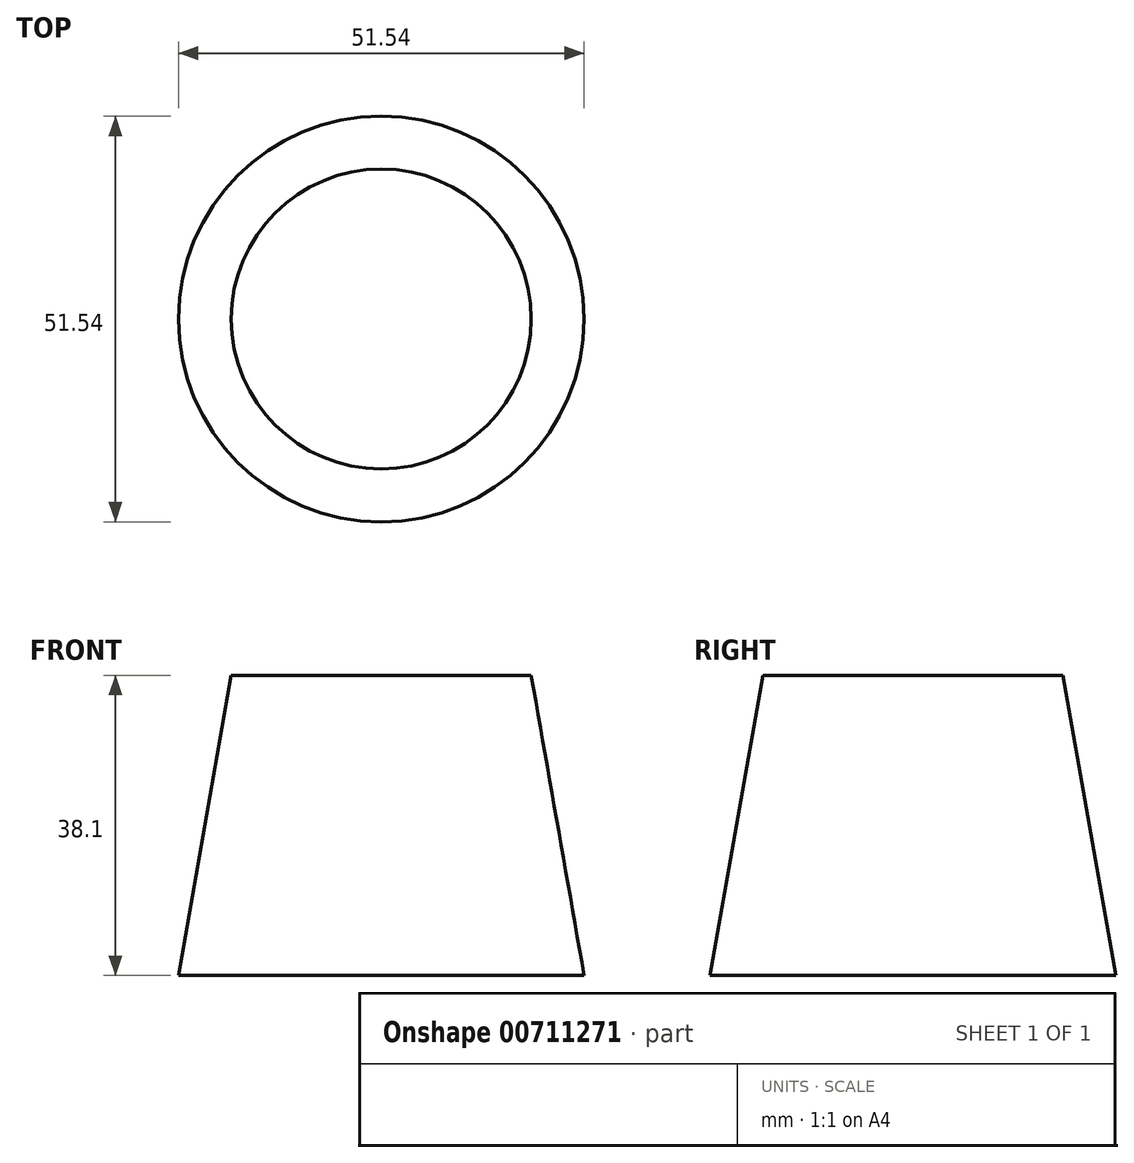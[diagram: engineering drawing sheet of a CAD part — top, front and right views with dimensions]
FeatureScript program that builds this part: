
annotation { "Feature Type Name" : "Feature", "Feature Type Description" : "" }
export const myFeature = defineFeature(function(context is Context, id is Id, definition is map)
    precondition{}
    {
        {
            var Q0;
            Q0=qCreatedBy(makeId("Top.planeOp"),FACE);
            var sketch = newSketch(context, id + "F0", { "sketchPlane" : qUnion([Q0])});
            skCircle(sketch, "E0", {"center": v(0, 0) * mm, "radius": 19.05 * mm});
            skSolve(sketch);
        }
        {
            var Q0;
            Q0=makeQuery(id+"F0.imprint","IMPRINT",FACE,{"disambiguationData":[TD([[makeQuery(id+"F0.imprint","IMPRINT",EDGE,{"derivedFrom":sQuery(id+"F0.wireOp",EDGE,"E0")}),1.0]])]});
            extrude(context, id + "F1", {"entities" : qUnion([Q0]), "oppositeDirection" : true, "depth" : 38.1 * mm, "offsetDistance" : 25.4 * mm, "hasDraft" : true, "draftAngle" : 10 * degree});
        }
    });
